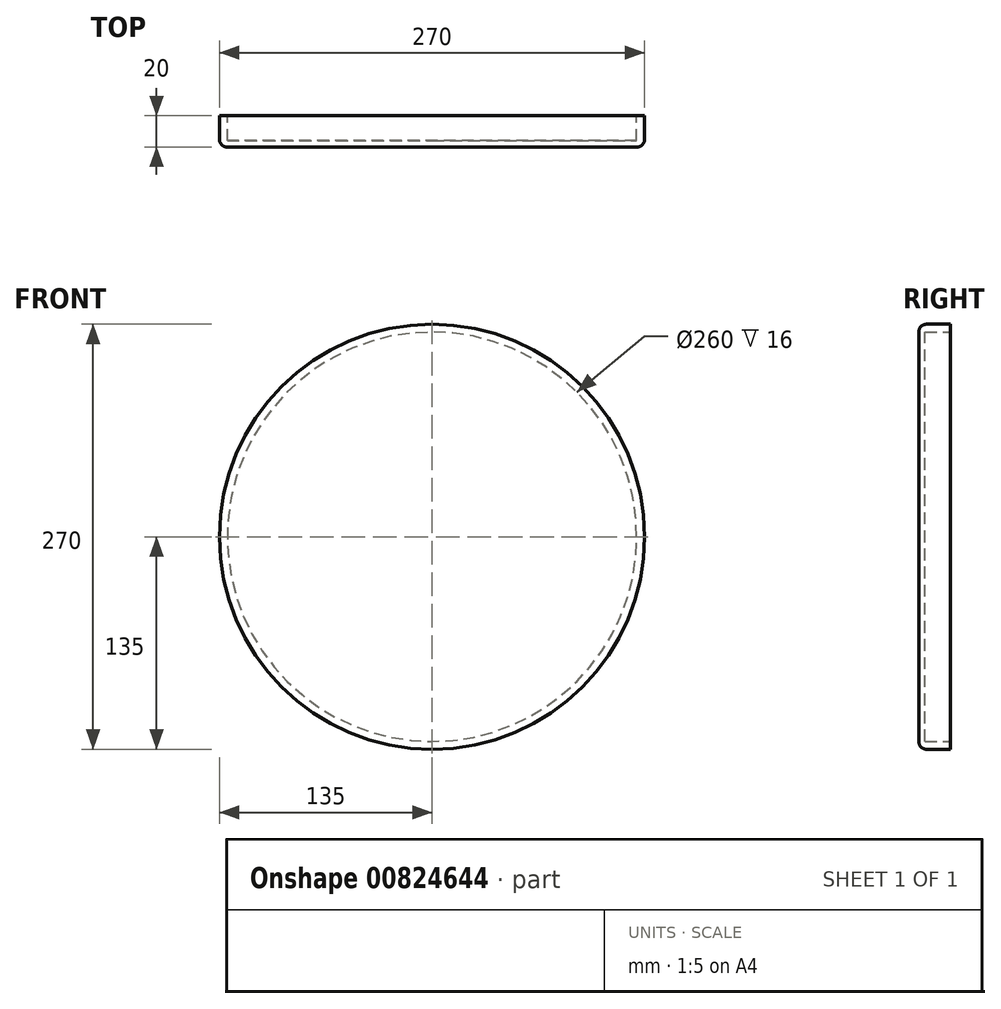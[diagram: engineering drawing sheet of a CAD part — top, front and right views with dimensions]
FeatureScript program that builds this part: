
annotation { "Feature Type Name" : "Feature", "Feature Type Description" : "" }
export const myFeature = defineFeature(function(context is Context, id is Id, definition is map)
    precondition{}
    {
        {
            var Q0;
            Q0=qCreatedBy(makeId("Front.planeOp"),FACE);
            var sketch = newSketch(context, id + "F0", { "sketchPlane" : qUnion([Q0])});
            skCircle(sketch, "E0", {"center": v(0, 0) * mm, "radius": 135 * mm});
            skSolve(sketch);
        }
        {
            var Q0;
            Q0=makeQuery(id+"F0.imprint","IMPRINT",FACE,{"disambiguationData":[TD([[makeQuery(id+"F0.imprint","IMPRINT",EDGE,{"derivedFrom":sQuery(id+"F0.wireOp",EDGE,"E0")}),1.0]])]});
            var Q1;
            Q1=sQuery(id+"F0.wireOp",EDGE,"E0");
            extrude(context, id + "F1", {"entities" : qUnion([Q0]), "surfaceEntities" : qUnion([Q1]), "depth" : 20 * mm, "offsetDistance" : 25 * mm});
        }
        {
            var Q0;
            Q0=qCreatedBy(makeId("Front.planeOp"),FACE);
            var sketch = newSketch(context, id + "F2", { "sketchPlane" : qUnion([Q0])});
            skCircle(sketch, "E1", {"center": v(0, 0) * mm, "radius": 130 * mm});
            skSolve(sketch);
        }
        {
            var Q0;
            Q0 = qSketchRegion(id + "F2", true);
            extrude(context, id + "F3", {"entities" : qUnion([Q0]), "operationType" : NewBodyOperationType.REMOVE, "depth" : 16 * mm, "offsetDistance" : 25 * mm});
        }
        {
            var Q0;
            Q0=makeQuery(id+"F3.boolean.opBoolean","COPY",EDGE,{"derivedFrom":makeQuery(id+"F3.opExtrude","CAP_EDGE",EDGE,{"disambiguationData":[OSD([sQuery(id+"F2.wireOp",EDGE,"E1")])],"isStart":true})});
            var Q1;
            Q1=makeQuery(id+"F1.opExtrude","CAP_EDGE",EDGE,{"disambiguationData":[OSD([sQuery(id+"F0.wireOp",EDGE,"E0")])],"isStart":false});
            fillet(context, id + "F4", {"entities" : qUnion([Q0, Q1]), "radius" : 5 * mm, "tangentPropagation" : true, "allowEdgeOverflow" : false});
        }
    });
